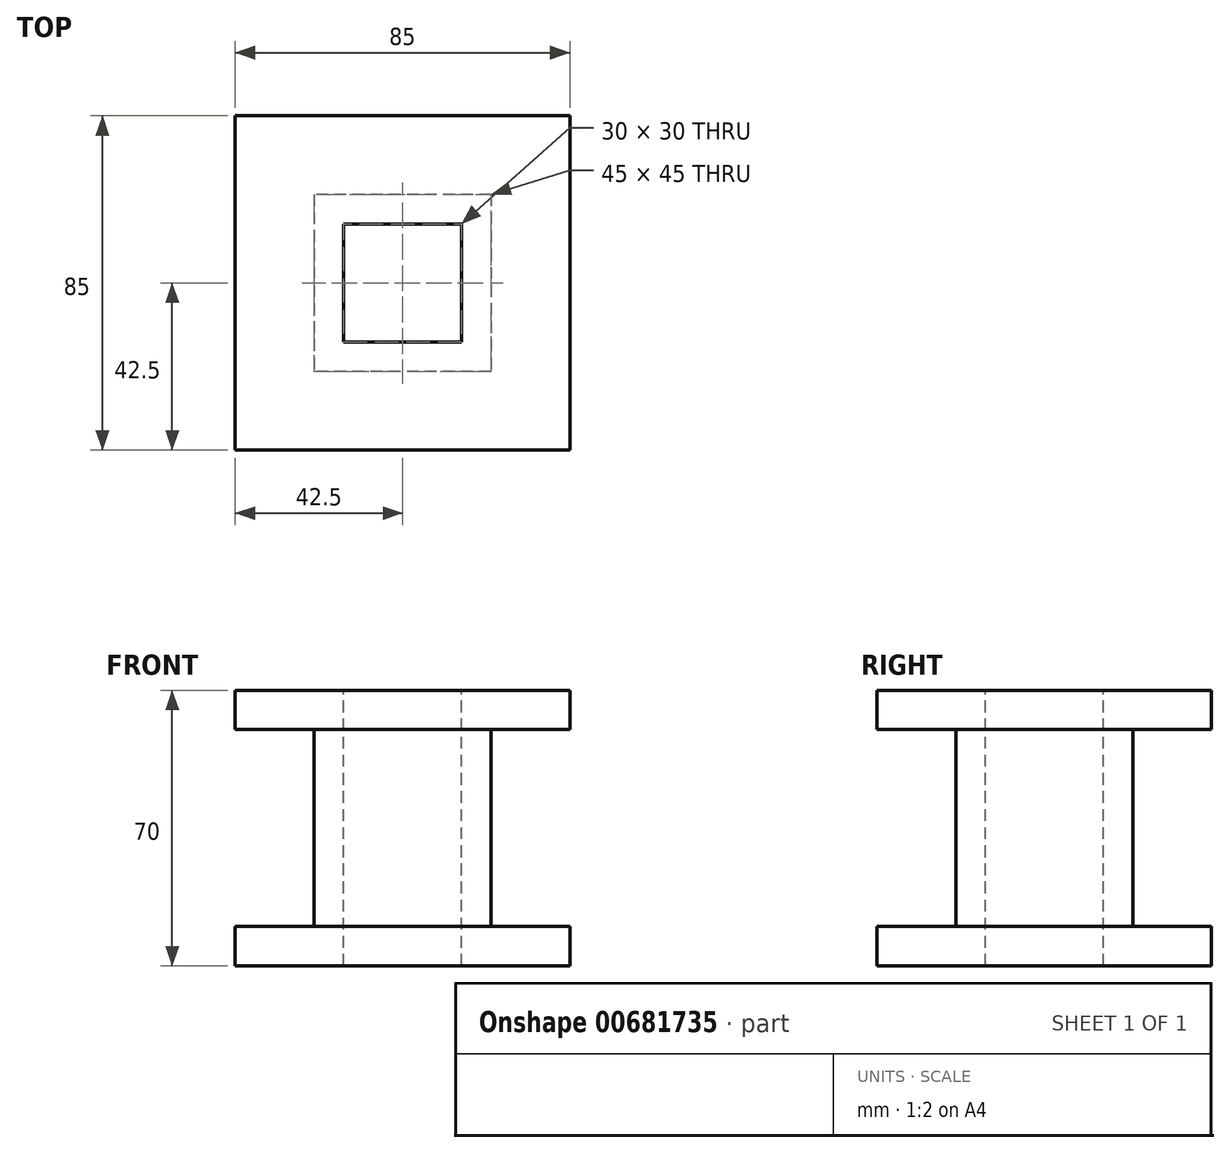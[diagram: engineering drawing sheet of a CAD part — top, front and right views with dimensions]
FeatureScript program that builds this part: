
annotation { "Feature Type Name" : "Feature", "Feature Type Description" : "" }
export const myFeature = defineFeature(function(context is Context, id is Id, definition is map)
    precondition{}
    {
        {
            var Q0;
            Q0=qCreatedBy(makeId("Top.planeOp"),FACE);
            var sketch = newSketch(context, id + "F0", { "sketchPlane" : qUnion([Q0])});
            skLineSegment(sketch, "E0.bottom", {"start": v(42.5, 42.5) * mm, "end": v(-42.5, 42.5) * mm});
            skLineSegment(sketch, "E0.top", {"start": v(42.5, -42.5) * mm, "end": v(-42.5, -42.5) * mm});
            skLineSegment(sketch, "E0.left", {"start": v(42.5, 42.5) * mm, "end": v(42.5, -42.5) * mm});
            skLineSegment(sketch, "E0.right", {"start": v(-42.5, 42.5) * mm, "end": v(-42.5, -42.5) * mm});
            skPoint(sketch, "E0.middle", {"position": v(0, 0) * mm});
            skSolve(sketch);
        }
        {
            var Q0;
            Q0 = qSketchRegion(id + "F0", true);
            extrude(context, id + "F1", {"entities" : qUnion([Q0]), "depth" : 10 * mm, "offsetDistance" : 25 * mm});
        }
        {
            var Q0;
            Q0=makeQuery(id+"F1.opExtrude","CAP_FACE",FACE,{"disambiguationData":[OSD([sQuery(id+"F0.wireOp",EDGE,"E0.bottom"),sQuery(id+"F0.wireOp",EDGE,"E0.top"),sQuery(id+"F0.wireOp",EDGE,"E0.left"),sQuery(id+"F0.wireOp",EDGE,"E0.right")])],"isStart":false});
            var sketch = newSketch(context, id + "F2", { "sketchPlane" : qUnion([Q0])});
            skLineSegment(sketch, "E1.bottom", {"start": v(22.5, 22.5) * mm, "end": v(-22.5, 22.5) * mm});
            skLineSegment(sketch, "E1.top", {"start": v(22.5, -22.5) * mm, "end": v(-22.5, -22.5) * mm});
            skLineSegment(sketch, "E1.left", {"start": v(22.5, 22.5) * mm, "end": v(22.5, -22.5) * mm});
            skLineSegment(sketch, "E1.right", {"start": v(-22.5, 22.5) * mm, "end": v(-22.5, -22.5) * mm});
            skPoint(sketch, "E1.middle", {"position": v(0, 0) * mm});
            skSolve(sketch);
        }
        {
            var Q0;
            Q0 = qSketchRegion(id + "F2", true);
            extrude(context, id + "F3", {"entities" : qUnion([Q0]), "operationType" : NewBodyOperationType.ADD, "depth" : 50 * mm, "offsetDistance" : 25 * mm});
        }
        {
            var Q0;
            Q0=makeQuery(id+"F3.opExtrude","CAP_FACE",FACE,{"disambiguationData":[OSD([sQuery(id+"F2.wireOp",EDGE,"E1.bottom"),sQuery(id+"F2.wireOp",EDGE,"E1.top"),sQuery(id+"F2.wireOp",EDGE,"E1.left"),sQuery(id+"F2.wireOp",EDGE,"E1.right")])],"isStart":false});
            var sketch = newSketch(context, id + "F4", { "sketchPlane" : qUnion([Q0])});
            skLineSegment(sketch, "E2.bottom", {"start": v(42.5, 42.5) * mm, "end": v(-42.5, 42.5) * mm});
            skLineSegment(sketch, "E2.top", {"start": v(42.5, -42.5) * mm, "end": v(-42.5, -42.5) * mm});
            skLineSegment(sketch, "E2.left", {"start": v(42.5, 42.5) * mm, "end": v(42.5, -42.5) * mm});
            skLineSegment(sketch, "E2.right", {"start": v(-42.5, 42.5) * mm, "end": v(-42.5, -42.5) * mm});
            skPoint(sketch, "E2.middle", {"position": v(0, 0) * mm});
            skSolve(sketch);
        }
        {
            var Q0;
            Q0 = qSketchRegion(id + "F4", true);
            extrude(context, id + "F5", {"entities" : qUnion([Q0]), "operationType" : NewBodyOperationType.ADD, "depth" : 10 * mm, "offsetDistance" : 25 * mm});
        }
        {
            var Q0;
            Q0=makeQuery(id+"F5.opExtrude","CAP_FACE",FACE,{"disambiguationData":[OSD([sQuery(id+"F4.wireOp",EDGE,"E2.bottom"),sQuery(id+"F4.wireOp",EDGE,"E2.top"),sQuery(id+"F4.wireOp",EDGE,"E2.left"),sQuery(id+"F4.wireOp",EDGE,"E2.right")])],"isStart":false});
            var sketch = newSketch(context, id + "F6", { "sketchPlane" : qUnion([Q0])});
            skLineSegment(sketch, "E3.bottom", {"start": v(15, 15) * mm, "end": v(-15, 15) * mm});
            skLineSegment(sketch, "E3.top", {"start": v(15, -15) * mm, "end": v(-15, -15) * mm});
            skLineSegment(sketch, "E3.left", {"start": v(15, 15) * mm, "end": v(15, -15) * mm});
            skLineSegment(sketch, "E3.right", {"start": v(-15, 15) * mm, "end": v(-15, -15) * mm});
            skPoint(sketch, "E3.middle", {"position": v(0, 0) * mm});
            skSolve(sketch);
        }
        {
            var Q0;
            Q0 = qSketchRegion(id + "F6", true);
            extrude(context, id + "F7", {"entities" : qUnion([Q0]), "operationType" : NewBodyOperationType.REMOVE, "oppositeDirection" : true, "depth" : 70 * mm, "offsetDistance" : 25 * mm});
        }
    });
